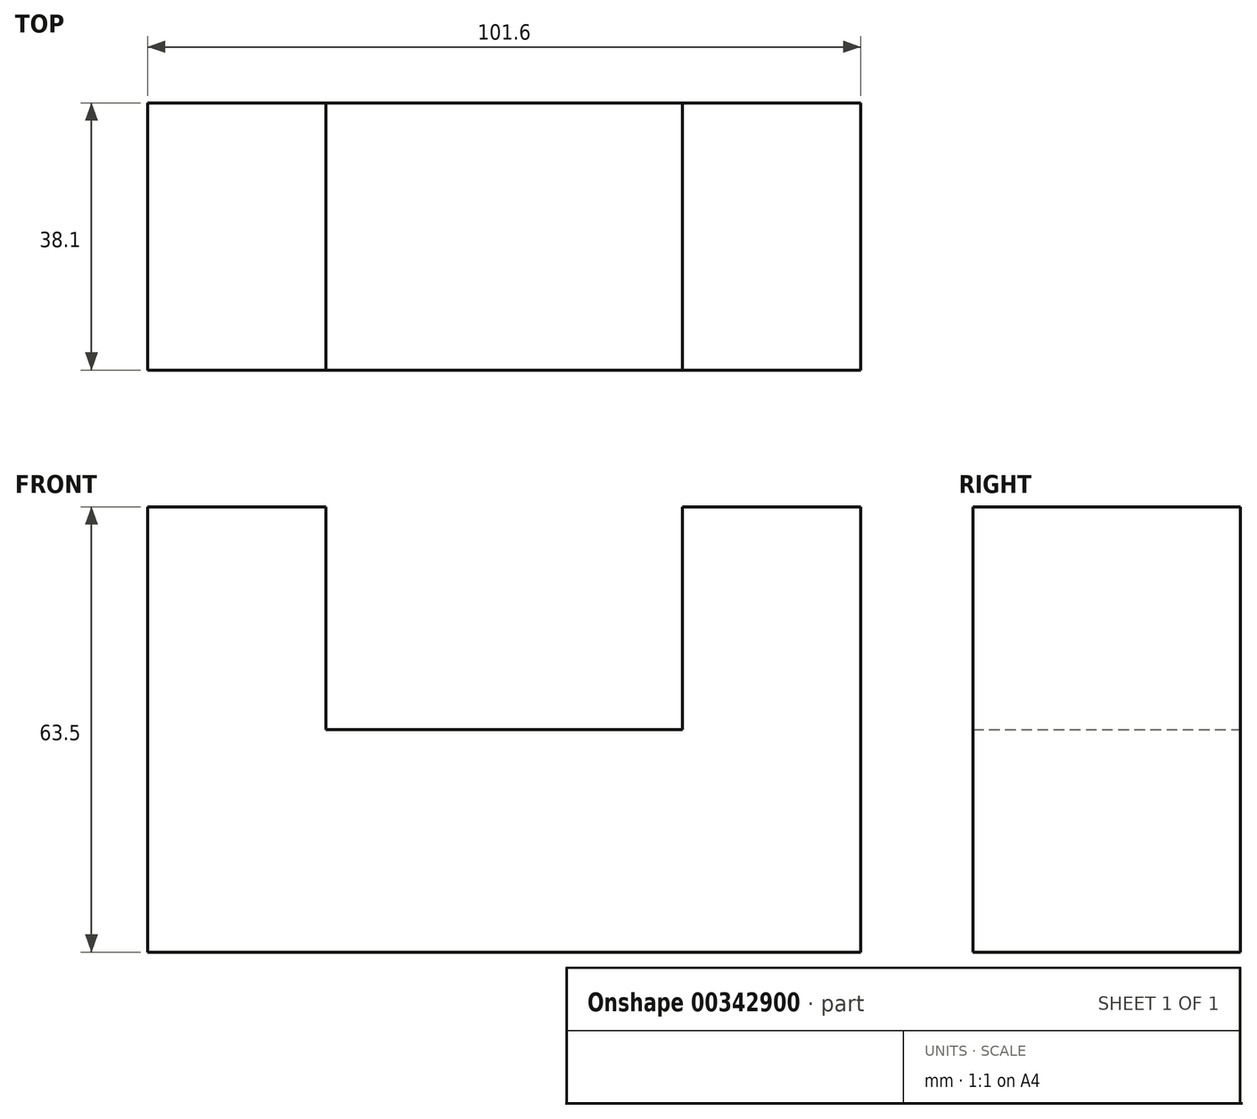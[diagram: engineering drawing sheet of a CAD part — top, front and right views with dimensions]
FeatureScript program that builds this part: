
annotation { "Feature Type Name" : "Feature", "Feature Type Description" : "" }
export const myFeature = defineFeature(function(context is Context, id is Id, definition is map)
    precondition{}
    {
        {
            var Q0;
            Q0=qCreatedBy(makeId("Front.planeOp"),FACE);
            var sketch = newSketch(context, id + "F0", { "sketchPlane" : qUnion([Q0])});
            skLineSegment(sketch, "E0", {"start": v(-65.87, -39.79) * mm, "end": v(35.73, -39.79) * mm});
            skLineSegment(sketch, "E1", {"start": v(35.73, -39.79) * mm, "end": v(35.73, 23.71) * mm});
            skLineSegment(sketch, "E2", {"start": v(35.73, 23.71) * mm, "end": v(10.33, 23.71) * mm});
            skLineSegment(sketch, "E3", {"start": v(10.33, 23.71) * mm, "end": v(10.33, -8.04) * mm});
            skLineSegment(sketch, "E4", {"start": v(10.33, -8.04) * mm, "end": v(-40.47, -8.04) * mm});
            skLineSegment(sketch, "E5", {"start": v(-40.47, -8.04) * mm, "end": v(-40.47, 23.71) * mm});
            skLineSegment(sketch, "E6", {"start": v(-40.47, 23.71) * mm, "end": v(-65.87, 23.71) * mm});
            skLineSegment(sketch, "E7", {"start": v(-65.87, 23.71) * mm, "end": v(-65.87, -39.79) * mm});
            skSolve(sketch);
        }
        {
            var Q0;
            Q0 = qSketchRegion(id + "F0", true);
            extrude(context, id + "F1", {"entities" : qUnion([Q0]), "depth" : 38.1 * mm});
        }
    });
